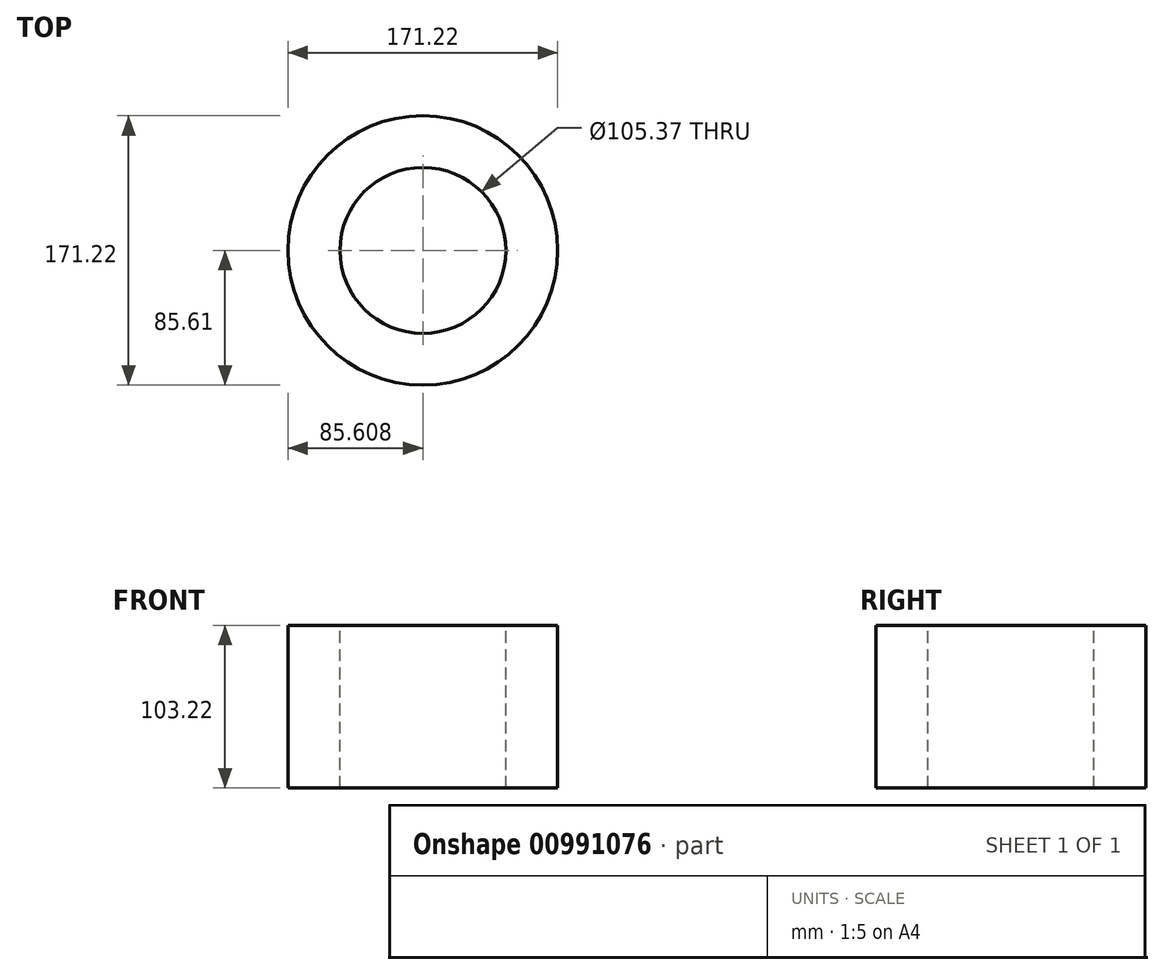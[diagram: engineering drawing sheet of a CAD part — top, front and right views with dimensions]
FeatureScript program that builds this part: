
annotation { "Feature Type Name" : "Feature", "Feature Type Description" : "" }
export const myFeature = defineFeature(function(context is Context, id is Id, definition is map)
    precondition{}
    {
        {
            var Q0;
            Q0=qCreatedBy(makeId("Front.planeOp"),FACE);
            var sketch = newSketch(context, id + "F0", { "sketchPlane" : qUnion([Q0])});
            skLineSegment(sketch, "E0", {"start": v(34.85, 46.98) * mm, "end": v(34.85, -46) * mm});
            skLineSegment(sketch, "E1.bottom", {"start": v(-50.76, 50.83) * mm, "end": v(-17.84, 50.83) * mm});
            skLineSegment(sketch, "E1.top", {"start": v(-50.76, -52.39) * mm, "end": v(-17.84, -52.39) * mm});
            skLineSegment(sketch, "E1.left", {"start": v(-50.76, 50.83) * mm, "end": v(-50.76, -52.39) * mm});
            skLineSegment(sketch, "E1.right", {"start": v(-17.84, 50.83) * mm, "end": v(-17.84, -52.39) * mm});
            skSolve(sketch);
        }
        {
            var Q0;
            Q0=makeQuery(id+"F0.imprint","IMPRINT",FACE,{"disambiguationData":[TD([[makeQuery(id+"F0.imprint","IMPRINT",EDGE,{"derivedFrom":sQuery(id+"F0.wireOp",EDGE,"E1.bottom")}),-1.0]])]});
            var Q1;
            Q1=sQuery(id+"F0.wireOp",EDGE,"E0");
            revolve(context, id + "F1", {"surfaceOperationType" : NewSurfaceOperationType.NEW, "entities" : qUnion([Q0]), "axis" : qUnion([Q1]), "revolveType" : RevolveType.FULL});
        }
    });
